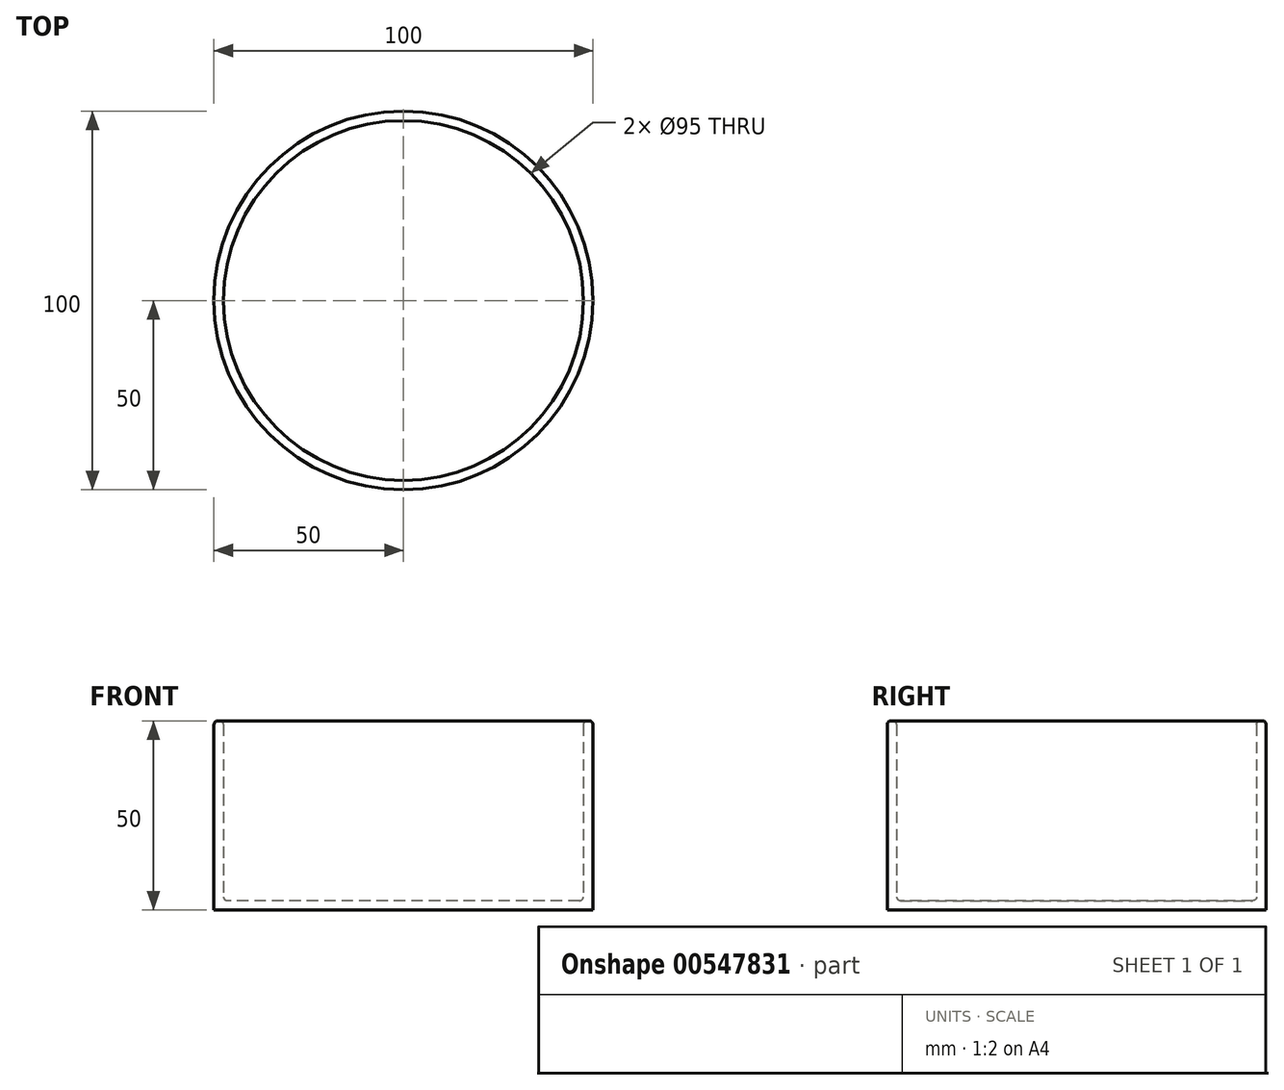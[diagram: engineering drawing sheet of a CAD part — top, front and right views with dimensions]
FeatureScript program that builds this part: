
annotation { "Feature Type Name" : "Feature", "Feature Type Description" : "" }
export const myFeature = defineFeature(function(context is Context, id is Id, definition is map)
    precondition{}
    {
        {
            var Q0;
            Q0=qCreatedBy(makeId("Top.planeOp"),FACE);
            var sketch = newSketch(context, id + "F0", { "sketchPlane" : qUnion([Q0])});
            skCircle(sketch, "E0", {"center": v(0, 0) * mm, "radius": 50 * mm});
            skSolve(sketch);
        }
        {
            var Q0;
            Q0 = qSketchRegion(id + "F0", true);
            extrude(context, id + "F1", {"entities" : qUnion([Q0]), "depth" : 50 * mm, "offsetDistance" : 25 * mm});
        }
        {
            var Q0;
            Q0=makeQuery(id+"F1.opExtrude","CAP_FACE",FACE,{"disambiguationData":[OSD([sQuery(id+"F0.wireOp",EDGE,"E0")])],"isStart":false});
            shell(context, id + "F2", {"entities" : qUnion([Q0]), "thickness" : 2.5 * mm});
        }
        {
            var Q0;
            Q0=makeQuery(id+"F1.opExtrude","CAP_EDGE",EDGE,{"disambiguationData":[OSD([sQuery(id+"F0.wireOp",EDGE,"E0")])],"isStart":false});
            var Q1;
            {var subQ0=sQuery(id+"F0.wireOp",EDGE,"E0");Q1=makeQuery(id+"F2.opShell","OFFSET_EDGE",EDGE,{"disambiguationData":[OSD([subQ0]),TDD([makeQuery(id+"F1.opExtrude","CAP_EDGE",EDGE,{"disambiguationData":[OSD([subQ0])],"isStart":false})])]});}
            var Q2;
            {var subQ0=sQuery(id+"F0.wireOp",EDGE,"E0");Q2=makeQuery(id+"F2.opShell","OFFSET_EDGE",EDGE,{"disambiguationData":[OSD([subQ0]),TDD([makeQuery(id+"F1.opExtrude","CAP_EDGE",EDGE,{"disambiguationData":[OSD([subQ0])],"isStart":true})])]});}
            fillet(context, id + "F3", {"entities" : qUnion([Q0, Q1, Q2]), "radius" : 1 * mm, "tangentPropagation" : true, "allowEdgeOverflow" : false});
        }
    });
